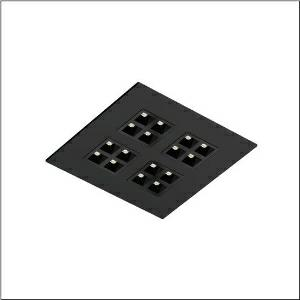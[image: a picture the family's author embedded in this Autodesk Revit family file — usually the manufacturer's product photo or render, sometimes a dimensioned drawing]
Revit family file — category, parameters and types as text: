
# Revit family: silica_r__31_square_51my6lms44ba_662e
name_source: partatom
category: Lighting Fixtures
units: mm (PartAtom-declared; Revit-internal decimal feet)

## family parameters
Cut with Voids When Loaded = No
Host = Face
Light Source = No
Part Type = Normal
Room Calculation Point = No
Round Connector Dimension = Use Diameter
Shared = No

## types (1)
- --- (1 x LED, 6620 lm, 39 W, 4000K)
    Apparent Load = 39 VA
    CIE Flux Codes = 82 100 100 100 100
    Color Rendering = 80
    Color Temperature = 4000K
    Default Elevation = 1800 mm
    Description = Silica® 31 Square, office luminaire, primary light control with lens, of PMMA, primary anti-glare with reflector, of PC, black, light emission: direct distribution, primary light characteristic: symmetric, installation type: lay-in mounting, LED, rated luminous flux: 4.610lm, luminous efficacy: 177lm/W, light colour: 840, colour temperature: 4000K, control gear: ON/OFF Multilumen, with terminal, 3-pole, mains connection: 220..240V, AC, 50/60Hz, rated input power: 26W, luminaire housing, of sheet steel, coated, jet black (RAL 9005), module: M600, length: 595mm, width: 595mm, height: 43mm, protection rating (complete): IP20, insulation class (complete): insulation class II (safety insulation), certification: CE, impact resistance: IK03, permissible operating ambient temperature: -20..+35°C, standard: EN 50419, packaging unit: 1 piece
    Height = 0 mm  [stored 0 ft]
    Lamp = 1 x LED
    Lamp Light Flux = 6620 lm
    Lamp Power = 39 W
    Lamp count = 1
    Length = 595 mm
    Luminous efficacy = 170 lm/W
    Manufacturer = Siteco
    ModVariant = No
    Model = 51MY6LMS44BA
    Mounting Place = Ceiling
    Mounting Type = Recessed
    Number of Poles = 1
    OnlyDefault = Yes
    Power Factor = 1
    Product Name = Silica® 31 Square
    Product group = office luminaire | ceiling recessed
    ProductGroupID = 401
    Protection Class = Protection class II
    Protection Degree = IP 20
    RLX_Detail_Level = 1
    RLX_Emergency_Light_Flux = 0 lm
    RLX_Emergency_Type = 0
    RLX_Emergency_Type_DB = No
    RlxData = <blob elided: 36181 chars, md5=064d9a8a>
    Socket = socket
    Standby Power = 0 W
    System Light Flux = 6620 lm
    System Power = 39 W
    Type Comments = factory setting: luminous flux: 100 % | (ON | ON | ON | ON) | 1100 mA
    Type Image = l_1313660.jpg
    URL = http://relux.com
    VarID = @adj_036204
    Voltage = 0 V
    Weight = 0.00 kg
    Width = 595 mm

note: [stored X ft] marks values corroborated as IEEE doubles in the binary element streams (Revit-internal decimal feet)

## geometry (parser evidence)
native form markers: Blend x4, Sweep x10
no freeform markers — native parametric forms only
